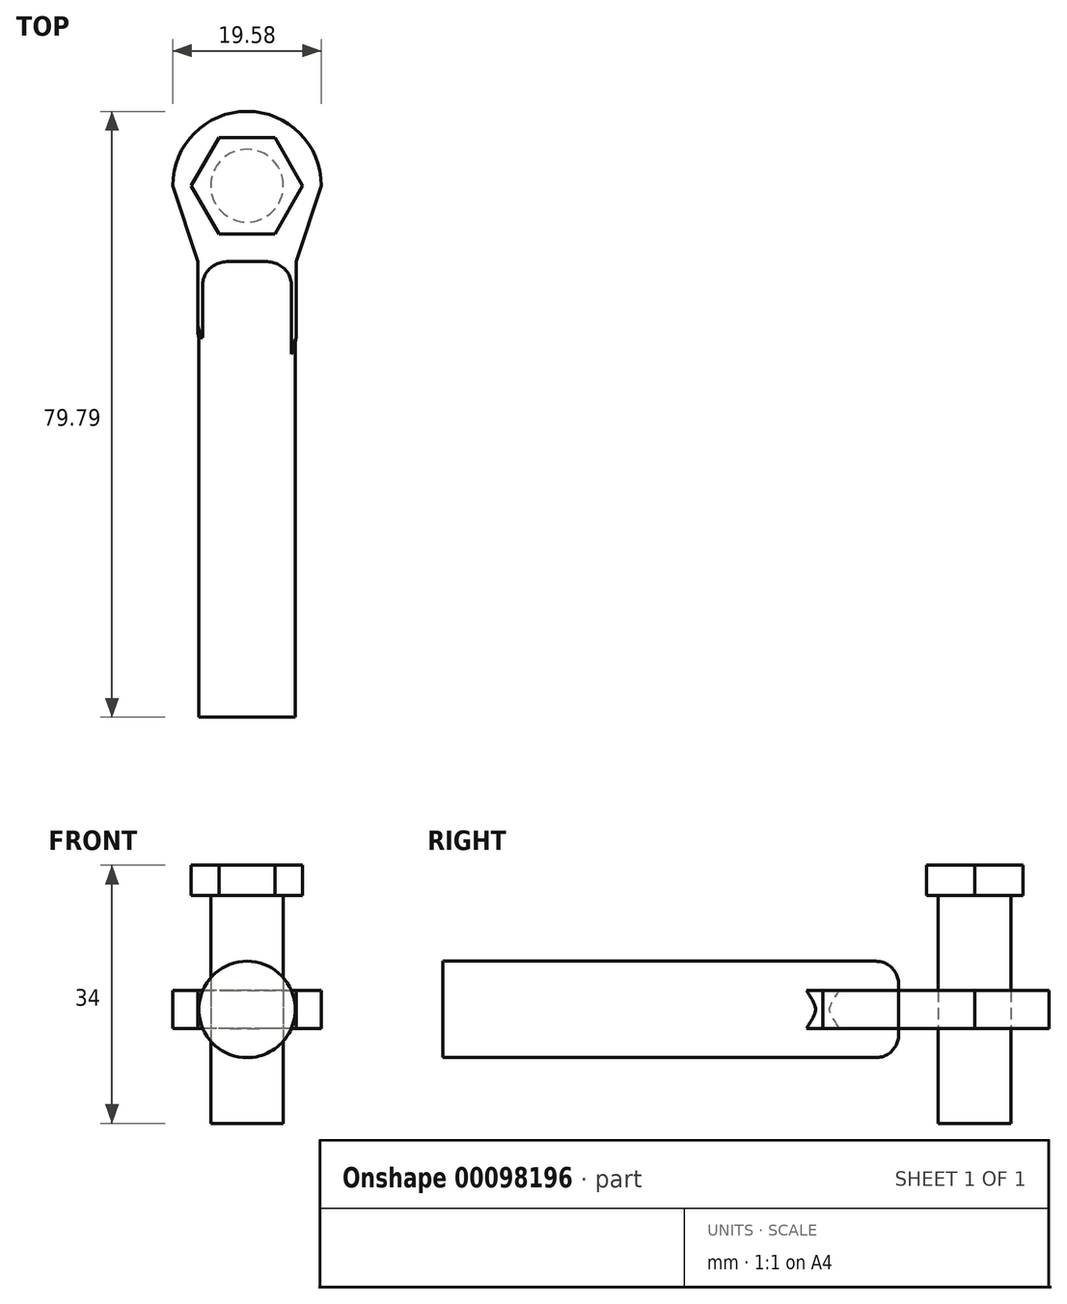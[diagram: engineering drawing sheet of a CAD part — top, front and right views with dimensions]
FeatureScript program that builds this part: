
annotation { "Feature Type Name" : "Feature", "Feature Type Description" : "" }
export const myFeature = defineFeature(function(context is Context, id is Id, definition is map)
    precondition{}
    {
        {
            var Q0;
            Q0=qCreatedBy(makeId("Top.planeOp"),FACE);
            var sketch = newSketch(context, id + "F0", { "sketchPlane" : qUnion([Q0])});
            skCircle(sketch, "E0", {"center": v(0, 0) * mm, "radius": 4.8 * mm});
            skLineSegment(sketch, "E1", {"start": v(-6.5, -20) * mm, "end": v(-6.5, -10) * mm});
            skLineSegment(sketch, "E2", {"start": v(6.5, -20) * mm, "end": v(6.5, -10) * mm});
            skLineSegment(sketch, "E3", {"start": v(-6.5, -20) * mm, "end": v(6.5, -20) * mm});
            skLineSegment(sketch, "E4", {"start": v(-6.5, -10) * mm, "end": v(-9.8, 0) * mm});
            skLineSegment(sketch, "E5", {"start": v(6.5, -10) * mm, "end": v(9.8, 0) * mm});
            skArc(sketch, "E6", {"start": v(-9.8, 0) * mm, "mid": v(0, 9.8) * mm, "end": v(9.8, 0) * mm});
            skSolve(sketch);
        }
        {
            var Q0;
            Q0=makeQuery(id+"F0.imprint","IMPRINT",FACE,{"disambiguationData":[TD([[makeQuery(id+"F0.imprint","IMPRINT",EDGE,{"derivedFrom":sQuery(id+"F0.wireOp",EDGE,"E0")}),-1.0]])]});
            extrude(context, id + "F1", {"entities" : qUnion([Q0]), "endBound" : BoundingType.SYMMETRIC, "depth" : 5 * mm});
        }
        {
            var Q0;
            Q0=makeQuery(id+"F1.opExtrude","SWEPT_FACE",FACE,{"disambiguationData":[OSD([sQuery(id+"F0.wireOp",EDGE,"E3")])]});
            var sketch = newSketch(context, id + "F2", { "sketchPlane" : qUnion([Q0])});
            skCircle(sketch, "E7", {"center": v(0, 0) * mm, "radius": 6.35 * mm});
            skSolve(sketch);
        }
        {
            var Q0;
            Q0=qSketchRegion(id+"F2",true);
            extrude(context, id + "F3", {"entities" : qUnion([Q0]), "operationType" : NewBodyOperationType.ADD, "depth" : 50 * mm, "hasSecondDirection" : true, "secondDirectionOppositeDirection" : true, "secondDirectionDepth" : 10 * mm});
        }
        {
            var Q0;
            {var subQ0=sQuery(id+"F2.wireOp",EDGE,"E7");Q0=makeQuery(id+"F3.boolean.opBoolean","SPLIT",EDGE,{"disambiguationData":[TD([makeQuery(id+"F1.opExtrude","CAP_FACE",FACE,{"disambiguationData":[OSD([sQuery(id+"F0.wireOp",EDGE,"E0"),sQuery(id+"F0.wireOp",EDGE,"E1"),sQuery(id+"F0.wireOp",EDGE,"E2"),sQuery(id+"F0.wireOp",EDGE,"E3"),sQuery(id+"F0.wireOp",EDGE,"E4"),sQuery(id+"F0.wireOp",EDGE,"E5"),sQuery(id+"F0.wireOp",EDGE,"E6")])],"isStart":false})])],"derivedFrom":makeQuery(id+"F3.opExtrude","CAP_EDGE",EDGE,{"disambiguationData":[OSD([subQ0])],"isStart":true})});}
            var Q1;
            {var subQ0=sQuery(id+"F2.wireOp",EDGE,"E7");Q1=makeQuery(id+"F3.boolean.opBoolean","SPLIT",EDGE,{"disambiguationData":[TD([makeQuery(id+"F1.opExtrude","CAP_FACE",FACE,{"disambiguationData":[OSD([sQuery(id+"F0.wireOp",EDGE,"E0"),sQuery(id+"F0.wireOp",EDGE,"E1"),sQuery(id+"F0.wireOp",EDGE,"E2"),sQuery(id+"F0.wireOp",EDGE,"E3"),sQuery(id+"F0.wireOp",EDGE,"E4"),sQuery(id+"F0.wireOp",EDGE,"E5"),sQuery(id+"F0.wireOp",EDGE,"E6")])],"isStart":true})])],"derivedFrom":makeQuery(id+"F3.opExtrude","CAP_EDGE",EDGE,{"disambiguationData":[OSD([subQ0])],"isStart":true})});}
            var Q2;
            Q2=makeQuery(id+"F3.boolean.opBoolean","INTERSECT",EDGE,{"disambiguationData":[OD(1.0)],"derivedFrom":[makeQuery(id+"F1.opExtrude","SWEPT_FACE",FACE,{"disambiguationData":[OSD([sQuery(id+"F0.wireOp",EDGE,"E3")])]}),makeQuery(id+"F3.opExtrude","SWEPT_FACE",FACE,{"disambiguationData":[OSD([sQuery(id+"F2.wireOp",EDGE,"E7")])]})]});
            var Q3;
            Q3=makeQuery(id+"F1.opExtrude","SWEPT_EDGE",EDGE,{"disambiguationData":[OSD([sQuery(id+"F0.wireOp",EDGE,"E1"),sQuery(id+"F0.wireOp",EDGE,"E3")])]});
            fillet(context, id + "F4", {"entities" : qUnion([Q0, Q1, Q2, Q3]), "radius" : 3 * mm, "tangentPropagation" : true, "allowEdgeOverflow" : false});
        }
        {
            var Q0;
            Q0=makeQuery(id+"F0.imprint","IMPRINT",FACE,{"disambiguationData":[TD([[makeQuery(id+"F0.imprint","IMPRINT",EDGE,{"derivedFrom":sQuery(id+"F0.wireOp",EDGE,"E0")}),1.0]])]});
            var Q1;
            Q1=sQuery(id+"F0.wireOp",EDGE,"E0");
            extrude(context, id + "F5", {"entities" : qUnion([Q0]), "surfaceEntities" : qUnion([Q1]), "endBound" : BoundingType.SYMMETRIC, "depth" : 30 * mm});
        }
        {
            var Q0;
            Q0=makeQuery(id+"F5.opExtrude","CAP_FACE",FACE,{"disambiguationData":[OSD([sQuery(id+"F0.wireOp",EDGE,"E0")])],"isStart":false});
            var sketch = newSketch(context, id + "F6", { "sketchPlane" : qUnion([Q0])});
            skCircle(sketch, "E8.cCircle", {"center": v(0, 0) * mm, "radius": 6.35 * mm, "construction": true});
            skLineSegment(sketch, "E8.0", {"start": v(7.33, 0) * mm, "end": v(3.67, -6.35) * mm});
            skLineSegment(sketch, "E8.1", {"start": v(3.67, -6.35) * mm, "end": v(-3.67, -6.35) * mm});
            skLineSegment(sketch, "E8.2", {"start": v(-3.67, -6.35) * mm, "end": v(-7.33, 0) * mm});
            skLineSegment(sketch, "E8.3", {"start": v(-7.33, 0) * mm, "end": v(-3.67, 6.35) * mm});
            skLineSegment(sketch, "E8.4", {"start": v(-3.67, 6.35) * mm, "end": v(3.67, 6.35) * mm});
            skLineSegment(sketch, "E8.5", {"start": v(3.67, 6.35) * mm, "end": v(7.33, 0) * mm});
            skPoint(sketch, "E8.0.midPoint", {"position": v(5.5, -3.18) * mm});
            skSolve(sketch);
        }
        {
            var Q0;
            Q0=qSketchRegion(id+"F6",true);
            extrude(context, id + "F7", {"entities" : qUnion([Q0]), "operationType" : NewBodyOperationType.ADD, "depth" : 4 * mm});
        }
    });
